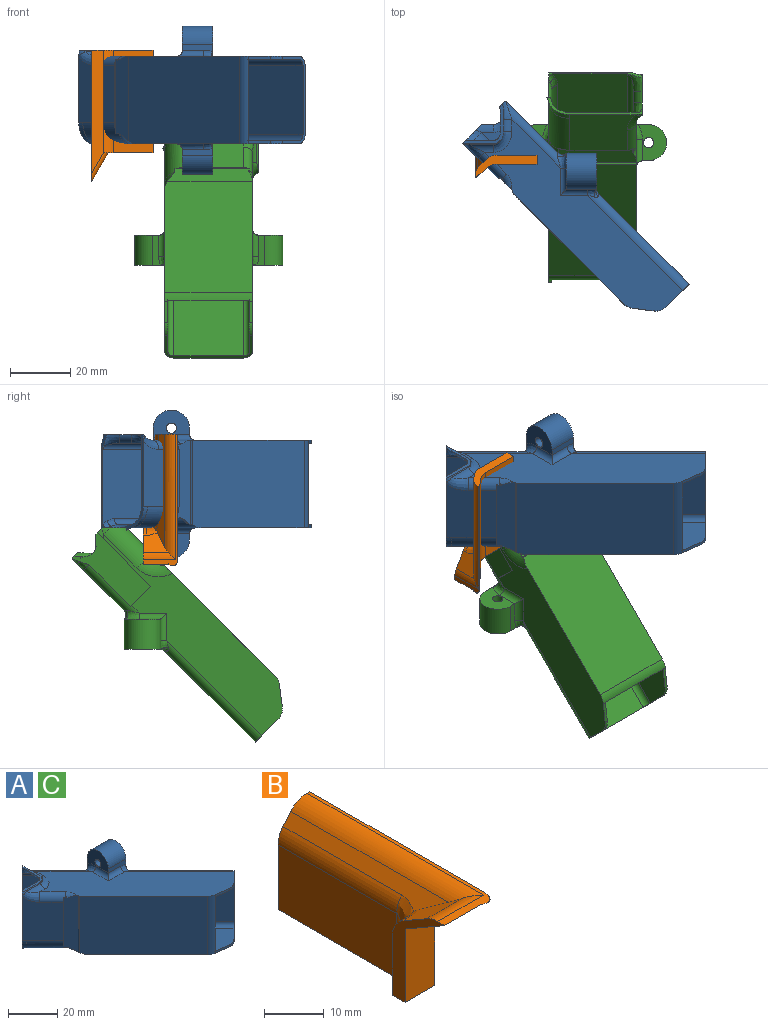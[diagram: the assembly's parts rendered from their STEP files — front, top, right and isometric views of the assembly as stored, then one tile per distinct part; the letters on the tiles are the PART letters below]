
ASSEMBLY  parts=3 mates=1
PART A: 119 faces, bbox 78.2x74.4x51.6 mm
  f0: cylinder r=3mm len=3.39mm, axis (1,0,0), area 3.5mm2, adj f7,f13,f22,f115
  f1: bspline ~2.8x2.8mm, area 0.2mm2, adj f6,f10,f116
  f2: cylinder r=4mm len=5.86mm, axis (1,0,0), area 14mm2, adj f11,f13,f29,f32,f116
  f3: cylinder r=4mm len=1.09mm, axis (0,1,0), area 0.5mm2, adj f4,f11,f116
  f4: bspline ~4.28x3.35mm, area 4.5mm2, adj f3,f5,f12,f14,f69,f116
  f5: bspline ~2.65x2.65mm, area 0.5mm2, adj f4,f12,f116
  f6: plane 27.88x0.73mm, normal (0,1,0), area 17.2mm2, adj f1,f10,f12,f21,f51,f53,f116
  f7: plane 66.53x59.19mm, normal (0,0,-1), area 987.9mm2, adj f0,f8,f35,f54,f60,f61,f96,f98
  f8: cylinder r=3mm len=18.5mm, axis (-0.71,0.71,0), area 85.9mm2, adj f7,f9,f51,f92,f94,f116,f117
  f9: bspline ~5.82x4.46mm, area 10.4mm2, adj f8,f10,f51,f116
  f10: bspline ~2.9x2.81mm, area 4.2mm2, adj f1,f6,f9,f51,f116
  f11: bspline ~6.93x6mm, area 20.6mm2, adj f2,f3,f32,f69,f116
  f12: plane 33.09x3.8mm, normal (-0.71,0.71,0), area 19.5mm2, adj f4,f5,f6,f14,f15,f16,f21,f28
  f13: plane 31.99x6.6mm, normal (-0.71,0.71,0), area 35.7mm2, adj f0,f2,f18,f20,f22,f23,f25,f27
  f14: plane 60.75x60.75mm, normal (-0.71,-0.71,0), area 1979.1mm2, adj f4,f12,f15,f35,f55,f69
  f15: cylinder r=2mm len=62.16mm, axis (0.71,-0.71,0), area 263.1mm2, adj f12,f14,f28,f33,f35
  f16: plane 0.56x0.31mm, normal (1,0,0), area 0.1mm2, adj f12,f21,f118
  f17: plane 8.45x0.39mm, normal (0,-0.87,0.5), area 3.7mm2, adj f19,f20,f57,f118
  f18: bspline ~8.03x5.91mm, area 25.2mm2, adj f13,f20,f43,f56,f57
  f19: cylinder r=3mm len=2.01mm, axis (0,0.5,0.87), area 0.5mm2, adj f17,f58,f118
  f20: cylinder r=3mm len=2.66mm, axis (-0.45,0.45,0.77), area 2.1mm2, adj f13,f17,f18,f118
  f21: bspline ~8.05x5.05mm, area 19.7mm2, adj f6,f12,f16,f53,f59,f118
  f22: bspline ~7.06x6.94mm, area 18.9mm2, adj f0,f13,f56,f60
  f23: plane 21.94x11.79mm, normal (0.71,0.71,0), area 323mm2, adj f13,f25,f29,f63,f67,f110
  f24: plane 8.73x0.89mm, normal (0,0.87,-0.5), area 8.7mm2, adj f26,f27,f64,f118
  f25: bspline ~7.32x5.91mm, area 17.9mm2, adj f13,f23,f27,f63,f64
  f26: cylinder r=2mm len=1.78mm, axis (0,0.5,0.87), area 1mm2, adj f24,f65,f118
  f27: cylinder r=2mm len=1.98mm, axis (-0.45,0.45,0.77), area 1.4mm2, adj f13,f24,f25,f118
  f28: bspline ~8.86x6.26mm, area 26.3mm2, adj f12,f15,f66,f118
  f29: bspline ~6.09x6.07mm, area 16.2mm2, adj f2,f13,f23,f67
  f30: plane 7.19x1mm, normal (-0.12,-0.99,0), area 7.2mm2, adj f31,f33,f113,f114
  f31: plane 65.53x63.31mm, normal (0,0,1), area 1190.8mm2, adj f30,f35,f36,f39,f40,f41,f43,f52
  f32: plane 66.53x63.69mm, normal (0,0,1), area 1153.9mm2, adj f2,f11,f34,f35,f55,f67,f68,f111
  f33: plane 65.53x63.31mm, normal (0,0,-1), area 1176.2mm2, adj f15,f30,f34,f35,f44,f62,f63,f64
  f34: plane 45.71x45.71mm, normal (0.71,0.71,0), area 1623.5mm2, adj f32,f33,f44,f62,f63,f67,f68,f110
  f35: plane 29x7.46mm, normal (0.71,-0.71,0), area 46mm2, adj f7,f14,f15,f31,f32,f33,f45,f52
  f36: cylinder r=6.39mm len=28mm, axis (0,0,-1), area 18.1mm2, adj f31,f39,f61,f109
  f37: plane 0.57x0.33mm, normal (0,0,-1), area 0.1mm2, adj f39,f61,f103
  f38: plane 0.45x0.45mm, normal (0.71,0.71,0), area 0mm2, adj f61,f103
  f39: plane 28.81x5.15mm, normal (-0.71,-0.71,0), area 159.6mm2, adj f31,f36,f37,f40,f41,f42,f99,f101
  f40: cylinder r=3mm len=0.98mm, axis (0,1,0), area 0.5mm2, adj f31,f39,f41
  f41: torus R=6mm, axis (0,0,1), area 7.4mm2, adj f31,f39,f40,f43,f108
  f42: plane 0.26x0.15mm, normal (-0.71,0.71,0), area 0mm2, adj f39,f43,f108
  f43: cylinder r=3mm len=9.39mm, axis (-0.71,0.71,0), area 46.6mm2, adj f18,f31,f41,f42,f56,f101,f108
  f44: cylinder r=2mm len=0.32mm, axis (0,1,0), area 0.1mm2, adj f33,f34,f62
  f45: plane 30.05x30.05mm, normal (0.71,0.71,0), area 977.3mm2, adj f35,f52,f54,f93
  f46: bspline ~2.64x2.62mm, area 2.4mm2, adj f50,f52,f89,f91
  f47: bspline ~2.64x2.62mm, area 2.4mm2, adj f50,f54,f95,f97
  f48: plane 12x9.44mm, normal (-1,0,0), area 73.7mm2, adj f49,f70,f71,f75,f94,f96
  f49: plane 10x2.46mm, normal (0,-1,0), area 20.4mm2, adj f48,f50,f70,f97,f98
  f50: plane 49.62x12.62mm, normal (1,0,0), area 286.2mm2, adj f46,f47,f49,f70,f71,f72,f73,f77
  f51: plane 24.46x17.03mm, normal (0.71,0.71,0), area 556.3mm2, adj f6,f8,f9,f10,f53,f90
  f52: cylinder r=3mm len=33.59mm, axis (0.71,-0.71,0), area 200.3mm2, adj f31,f35,f45,f46,f89,f91
  f53: cylinder r=3mm len=22.15mm, axis (0.71,-0.71,0), area 111.2mm2, adj f6,f21,f31,f51,f86,f88
  f54: cylinder r=3mm len=33.59mm, axis (-0.71,0.71,0), area 200.3mm2, adj f7,f35,f45,f47,f95,f97
  f55: cylinder r=2mm len=58.3mm, axis (-0.71,0.71,0), area 252.7mm2, adj f14,f32,f35,f69
  f56: plane 21.94x11.79mm, normal (-0.71,-0.71,0), area 323mm2, adj f13,f18,f22,f43,f60,f101
  f57: cylinder r=3mm len=8.22mm, axis (1,0,0), area 17.7mm2, adj f17,f18,f31,f58
  f58: bspline ~7.23x7.04mm, area 26.9mm2, adj f19,f31,f57,f59,f118
  f59: cylinder r=3mm len=3.85mm, axis (0,1,0), area 13.7mm2, adj f21,f31,f58,f118
  f60: cylinder r=7mm len=16.04mm, axis (0.71,-0.71,0), area 169.3mm2, adj f7,f22,f56,f61,f99,f101,f104
  f61: torus R=10mm, axis (0,0,-1), area 47.9mm2, adj f7,f36,f37,f38,f60,f100,f102,f106
  f62: torus R=6mm, axis (0,0,1), area 7.4mm2, adj f33,f34,f44,f63
  f63: cylinder r=2mm len=8.68mm, axis (-0.71,0.71,0), area 32.2mm2, adj f23,f25,f33,f34,f62,f110
  f64: cylinder r=4mm len=8.22mm, axis (1,0,0), area 23.6mm2, adj f24,f25,f33,f65
  f65: bspline ~7.23x7.04mm, area 33mm2, adj f26,f33,f64,f66,f118
  f66: cylinder r=4mm len=3.85mm, axis (0,1,0), area 19.8mm2, adj f28,f33,f65,f118
  f67: cylinder r=6mm len=15.33mm, axis (0.71,-0.71,0), area 147.6mm2, adj f23,f29,f32,f34,f68,f110
  f68: torus R=10mm, axis (0,0,-1), area 38.1mm2, adj f32,f34,f67
  f69: bspline ~5.2x4.29mm, area 8.7mm2, adj f4,f11,f14,f55
  f70: cylinder r=6mm len=12mm, axis (-1,0,0), area 188.5mm2, adj f48,f49,f50,f71
  f71: plane 37.41x10.41mm, normal (0,1,0), area 370mm2, adj f48,f50,f70,f72,f74,f88,f90,f92
  f72: cylinder r=6mm len=12mm, axis (-1,0,0), area 188.5mm2, adj f50,f71,f73,f74
  f73: plane 10x2.46mm, normal (0,-1,0), area 20.4mm2, adj f50,f72,f74,f87,f89
  f74: plane 12x9.44mm, normal (-1,0,0), area 73.7mm2, adj f71,f72,f73,f78,f85,f86
  f75: cylinder r=1.7mm len=7mm, axis (1,0,0), area 74.8mm2, adj f48,f76
  f76: plane 6.5x6.5mm, normal (1,0,0), area 24.1mm2, adj f75,f77
  f77: cylinder r=3.25mm len=6.5mm, axis (1,0,0), area 61.3mm2, adj f50,f76
  f78: cylinder r=1.7mm len=7mm, axis (1,0,0), area 74.8mm2, adj f74,f79
  f79: plane 6.5x6.5mm, normal (1,0,0), area 24.1mm2, adj f78,f80
  f80: cylinder r=3.25mm len=6.5mm, axis (1,0,0), area 61.3mm2, adj f50,f79
  f81: plane 28.35x8.19mm, normal (0.71,0.71,0), area 289.3mm2, adj f50,f82,f83,f84
  f82: plane 28.06x7.89mm, normal (0,-1,0), area 221.3mm2, adj f50,f81,f83,f84
  f83: cylinder r=6mm len=7.89mm, axis (1,0,0), area 33.9mm2, adj f50,f81,f82
  f84: cylinder r=6mm len=7.89mm, axis (1,0,0), area 33.9mm2, adj f50,f81,f82
  f85: cylinder r=2mm len=9.04mm, axis (0,1,0), area 25.3mm2, adj f31,f74,f86,f87
  f86: bspline ~4.96x3.06mm, area 16.1mm2, adj f53,f74,f85,f88
  f87: cylinder r=2mm len=9.04mm, axis (-1,0,0), area 25.3mm2, adj f31,f73,f85,f89
  f88: bspline ~4.41x3.13mm, area 8mm2, adj f53,f71,f86,f90
  f89: bspline ~4.11x3.48mm, area 8.9mm2, adj f46,f52,f73,f87
  f90: cylinder r=2mm len=23mm, axis (0,0,-1), area 70.4mm2, adj f51,f71,f88,f92
  f91: bspline ~3.63x2.3mm, area 4.8mm2, adj f46,f50,f52,f93
  f92: bspline ~4.41x3.13mm, area 8mm2, adj f8,f71,f90,f94
  f93: cylinder r=2mm len=23mm, axis (0,0,-1), area 33.5mm2, adj f45,f50,f91,f95
  f94: bspline ~4.96x3.06mm, area 16.1mm2, adj f8,f48,f92,f96
  f95: bspline ~3.63x2.3mm, area 4.8mm2, adj f47,f50,f54,f93
  f96: cylinder r=2mm len=9.04mm, axis (0,-1,0), area 25.3mm2, adj f7,f48,f94,f98
  f97: bspline ~2.96x2.59mm, area 8.9mm2, adj f47,f49,f54,f98
  f98: cylinder r=2mm len=9.04mm, axis (1,0,0), area 25.3mm2, adj f7,f49,f96,f97
  f99: plane 0.9x0.33mm, normal (-0.71,0.71,0), area 0.2mm2, adj f39,f60,f104
  f100: plane 0.82x0.82mm, normal (0.71,0.71,0), area 0mm2, adj f61,f105
  f101: plane 23.46x0.39mm, normal (0.71,-0.71,0), area 12.2mm2, adj f39,f43,f56,f60
  f102: plane 0.36x0.36mm, normal (-0.71,-0.71,0), area 0mm2, adj f61,f105
  f103: plane 2.67x2.67mm, normal (-0.35,0.35,-0.87), area 1.8mm2, adj f37,f38,f39,f106,f107
  f104: plane 0.91x0.91mm, normal (0,0,-1), area 0.4mm2, adj f39,f60,f99,f105
  f105: cylinder r=3.9mm len=1.5mm, axis (0.71,0.71,0), area 0.8mm2, adj f39,f100,f102,f104,f106
  f106: plane 0.33x0.33mm, normal (-0.33,0.33,-0.89), area 0mm2, adj f39,f61,f103,f105
  f107: plane 1.9x1.9mm, normal (-0.71,-0.71,0), area 0.1mm2, adj f61,f103
  f108: cylinder r=0.27mm len=1.24mm, axis (-0.71,0.71,0), area 0.5mm2, adj f39,f41,f42,f43
  f109: plane 36.8x36.8mm, normal (-0.71,-0.71,0), area 1507.8mm2, adj f7,f31,f36,f61,f114
  f110: cylinder r=10mm len=19.67mm, axis (0,0,-1), area 10.6mm2, adj f23,f34,f63,f67
  f111: plane 7.19x1mm, normal (-0.12,-0.99,0), area 7.2mm2, adj f7,f32,f112,f114
  f112: cylinder r=5mm len=4.16mm, axis (0,0,-1), area 4.5mm2, adj f7,f32,f35,f111
  f113: cylinder r=5mm len=4.16mm, axis (0,0,-1), area 4.5mm2, adj f30,f31,f33,f35
  f114: cylinder r=5mm len=29mm, axis (0,0,-1), area 94.2mm2, adj f7,f30,f31,f32,f33,f34,f109,f111
  f115: plane 17.82x17.82mm, normal (0.71,0.71,0), area 1.7mm2, adj f0,f7,f13,f116,f117
  f116: plane 26.17x24.72mm, normal (0,0,-1), area 220.5mm2, adj f1,f2,f3,f4,f5,f6,f8,f9
  f117: plane 6.72x6.72mm, normal (-0.71,0.71,0), area 0.4mm2, adj f7,f8,f115,f116
  f118: plane 14.01x13.85mm, normal (0,0,1), area 25.6mm2, adj f12,f13,f16,f17,f19,f20,f21,f24
PART B: 22 faces, bbox 12.8x44.7x21.8 mm
  f0: plane 9.29x8.5mm, normal (0,-0.5,-0.87), area 67mm2, adj f1,f2,f19,f21
  f1: plane 43.66x11.5mm, normal (0,0,1), area 46.7mm2, adj f0,f5,f8,f10,f18,f19,f21
  f2: plane 16.46x8.24mm, normal (0,-1,0), area 105.6mm2, adj f0,f7,f8,f9,f11,f19,f20,f21
  f3: plane 8.54x6.8mm, normal (0,0.5,0.87), area 44.8mm2, adj f4,f5,f6,f15,f18,f21
  f4: cylinder r=5mm len=4.33mm, axis (1,0,0), area 5.2mm2, adj f3,f12,f15,f21
  f5: cylinder r=5mm len=10.83mm, axis (1,0,0), area 25mm2, adj f1,f3,f18,f21
  f6: plane 37.26x3.34mm, normal (-0.77,0,0.64), area 103.5mm2, adj f3,f10,f15,f16,f17,f18
  f7: plane 2.96x1.07mm, normal (0,0,-1), area 0.6mm2, adj f2,f19
  f8: plane 41x4.04mm, normal (0.77,0,-0.64), area 194.6mm2, adj f1,f2,f10,f19,f20
  f9: plane 34x13.18mm, normal (1,0,0), area 448.1mm2, adj f2,f10,f11,f20
  f10: plane 20.36x7.5mm, normal (0,1,0), area 60.3mm2, adj f1,f6,f8,f9,f11,f13,f17,f18
  f11: plane 34x7mm, normal (0,0,-1), area 115.9mm2, adj f2,f9,f10,f12,f13,f14,f21
  f12: plane 12.11x1mm, normal (0,1,0), area 12.1mm2, adj f4,f11,f14,f21
  f13: plane 28x13.18mm, normal (-1,0,0), area 369mm2, adj f10,f11,f14,f17
  f14: cylinder r=3mm len=13.18mm, axis (0,0,1), area 54.8mm2, adj f11,f12,f13,f15,f16
  f15: bspline ~6.56x6.29mm, area 17.7mm2, adj f3,f4,f6,f14,f16
  f16: bspline ~5.76x5.44mm, area 14.5mm2, adj f6,f14,f15,f17
  f17: cylinder r=5mm len=28mm, axis (0,-1,0), area 97.7mm2, adj f6,f10,f13,f16
  f18: cylinder r=5mm len=41.66mm, axis (0,-1,0), area 172.4mm2, adj f1,f3,f5,f6,f10
  f19: cylinder r=3mm len=11.78mm, axis (-0.39,0.8,-0.46), area 44.7mm2, adj f0,f1,f2,f7,f8
  f20: cylinder r=5mm len=34mm, axis (0,-1,0), area 118.7mm2, adj f2,f8,f9,f10
  f21: plane 20.36x12.29mm, normal (-1,0,0), area 59.5mm2, adj f0,f1,f2,f3,f4,f5,f11,f12
PART C: same geometry as A
PLACE A t=(-185.17,-26.83,-3.91)mm
PLACE B rot(axis=(0.58,-0.58,-0.58),120deg) t=(-139.89,-51.98,21.13)mm
PLACE C rot(axis=(0,1,0),90deg) t=(-146.98,-17.29,31.86)mm
MATE fastened B.f12 <-> A.f116  axis (0,0,1) through (-145.94,-47.98,7.13)mm
